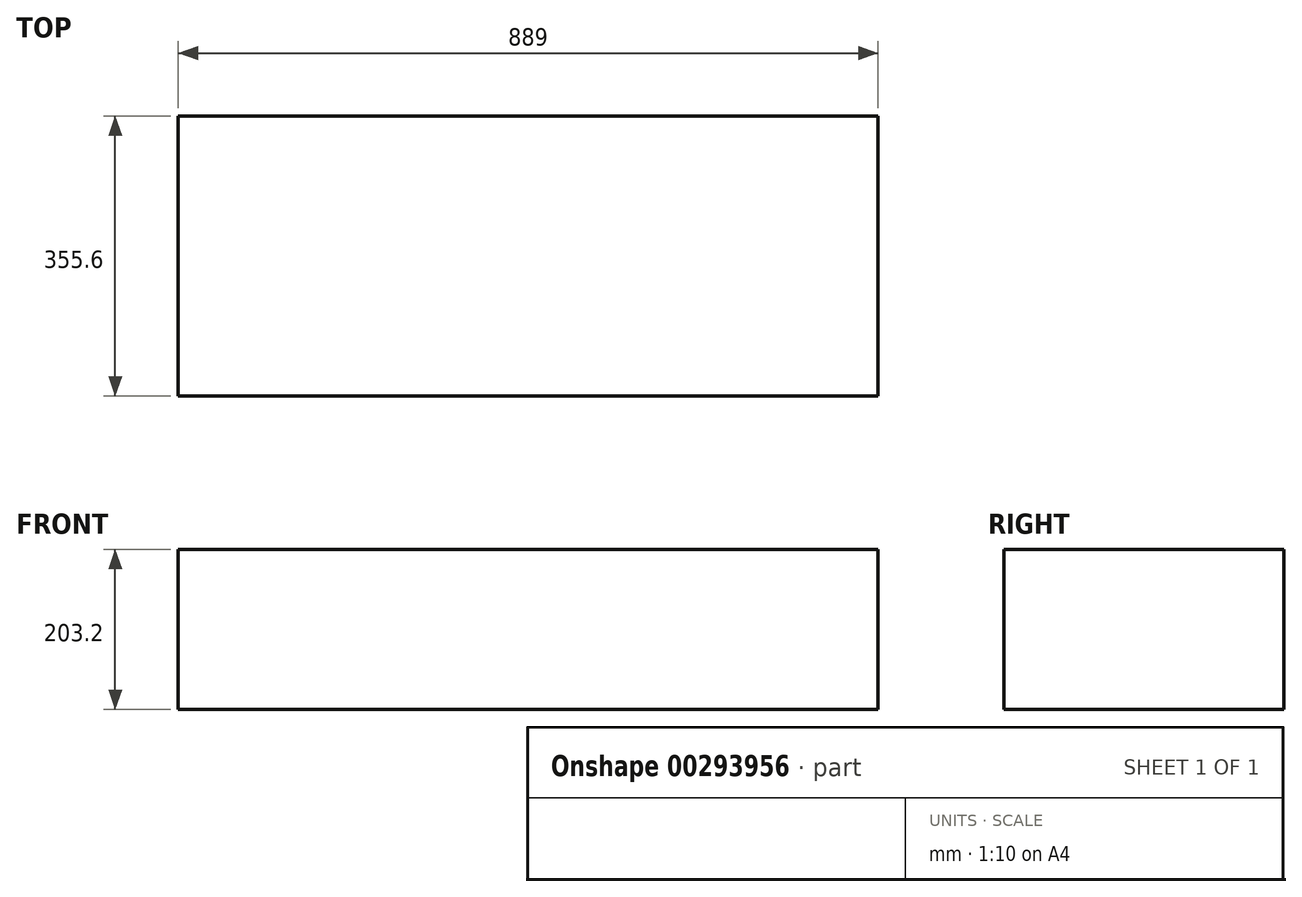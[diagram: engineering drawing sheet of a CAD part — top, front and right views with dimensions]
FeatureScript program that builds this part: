
annotation { "Feature Type Name" : "Feature", "Feature Type Description" : "" }
export const myFeature = defineFeature(function(context is Context, id is Id, definition is map)
    precondition{}
    {
        {
            var Q0;
            Q0=qCreatedBy(makeId("Top.planeOp"),FACE);
            var sketch = newSketch(context, id + "F0", { "sketchPlane" : qUnion([Q0])});
            skLineSegment(sketch, "E0.bottom", {"start": v(-444.5, -177.8) * mm, "end": v(444.5, -177.8) * mm});
            skLineSegment(sketch, "E0.top", {"start": v(-444.5, 177.8) * mm, "end": v(444.5, 177.8) * mm});
            skLineSegment(sketch, "E0.left", {"start": v(-444.5, -177.8) * mm, "end": v(-444.5, 177.8) * mm});
            skLineSegment(sketch, "E0.right", {"start": v(444.5, -177.8) * mm, "end": v(444.5, 177.8) * mm});
            skPoint(sketch, "E0.middle", {"position": v(0, 0) * mm});
            skSolve(sketch);
        }
        {
            var Q0;
            Q0 = qSketchRegion(id + "F0", true);
            extrude(context, id + "F1", {"entities" : qUnion([Q0]), "depth" : 203.2 * mm, "offsetDistance" : 25 * mm});
        }
    });
